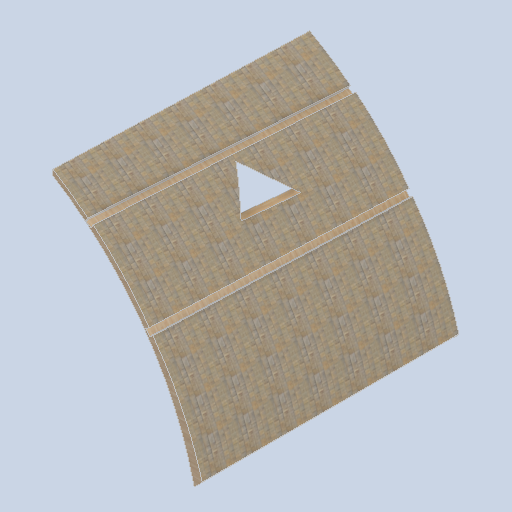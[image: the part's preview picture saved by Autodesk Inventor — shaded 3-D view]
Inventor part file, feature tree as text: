
AUTODESK INVENTOR PART (.ipt)
format: ipt  version: 2024.2 (Build 282272000, 272)  size: 370,688 bytes
history: native  units: in
note: dims shown in document units (in); Inventor stores cm internally (conversion verified against a paired STEP export)
features: other x3, sketch x2, plane x2
ambient origin geometry x8: Origin, YZ Plane, XZ Plane, XY Plane, X Axis, Y Axis, Z Axis, Center Point
bodies: Solid1 (feature_tree)
feature tree (7):
  other  "panel_block_03.ipt"
  other  "Solid1::panel_block_03.ipt"
  other  "TaggingFeature1"
  sketch  "Sketch1"  dims[d0=0.3937in]
  sketch  "Sketch2"
  plane  "Work Plane1"
  plane  "Work Plane2"
